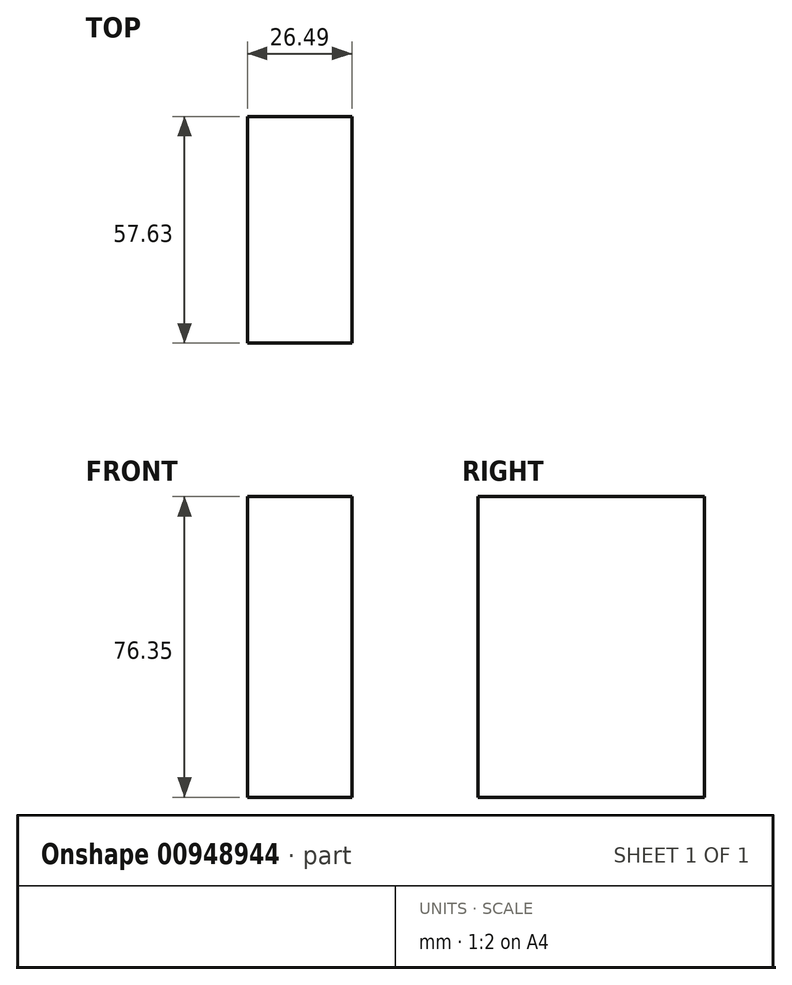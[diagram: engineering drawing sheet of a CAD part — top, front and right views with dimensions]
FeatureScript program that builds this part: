
annotation { "Feature Type Name" : "Feature", "Feature Type Description" : "" }
export const myFeature = defineFeature(function(context is Context, id is Id, definition is map)
    precondition{}
    {
        {
            var Q0;
            Q0=qCreatedBy(makeId("Front.planeOp"),FACE);
            var sketch = newSketch(context, id + "F0", { "sketchPlane" : qUnion([Q0])});
            skLineSegment(sketch, "E0.bottom", {"start": v(26.5, 76.35) * mm, "end": v(0, 76.35) * mm});
            skLineSegment(sketch, "E0.top", {"start": v(26.5, 0) * mm, "end": v(0, 0) * mm});
            skLineSegment(sketch, "E0.left", {"start": v(26.5, 76.35) * mm, "end": v(26.5, 0) * mm});
            skLineSegment(sketch, "E0.right", {"start": v(0, 76.35) * mm, "end": v(0, 0) * mm});
            skSolve(sketch);
        }
        {
            var Q0;
            Q0=makeQuery(id+"F0.imprint","IMPRINT",FACE,{"disambiguationData":[TD([[makeQuery(id+"F0.imprint","IMPRINT",EDGE,{"derivedFrom":sQuery(id+"F0.wireOp",EDGE,"E0.bottom")}),1.0]])]});
            extrude(context, id + "F1", {"entities" : qUnion([Q0]), "depth" : 57.63 * mm, "offsetDistance" : 25.4 * mm});
        }
    });
